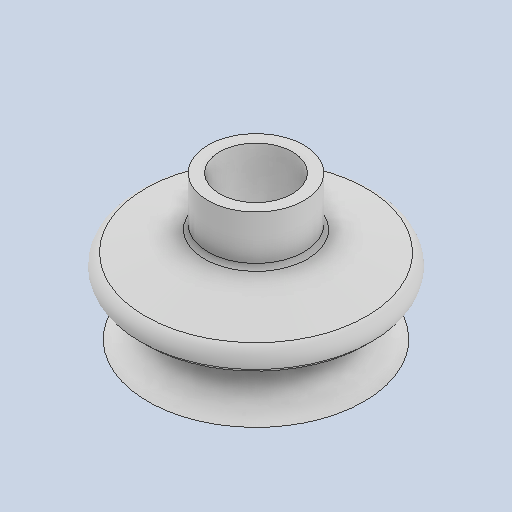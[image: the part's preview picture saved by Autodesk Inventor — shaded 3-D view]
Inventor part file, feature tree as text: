
AUTODESK INVENTOR PART (.ipt)
format: ipt  version: 2024 (Build 280153000, 153)  size: 205,824 bytes
history: native  units: mm
features: other x4, sketch x4
ambient origin geometry x8: Origin, YZ Plane, XZ Plane, XY Plane, X Axis, Y Axis, Z Axis, Center Point
bodies: Body1 (feature_tree)
feature tree (8):
  other  "VENTOSA_B.ipt"
  other  "Sólido1::VENTOSA_B.ipt"
  other  "OperaciónIdentificador1"
  sketch  "Boceto1"  dims[d0=10.0mm]
  sketch  "Boceto2"
  sketch  "Boceto3"
  sketch  "Boceto6"
  other  "Sólido1"
